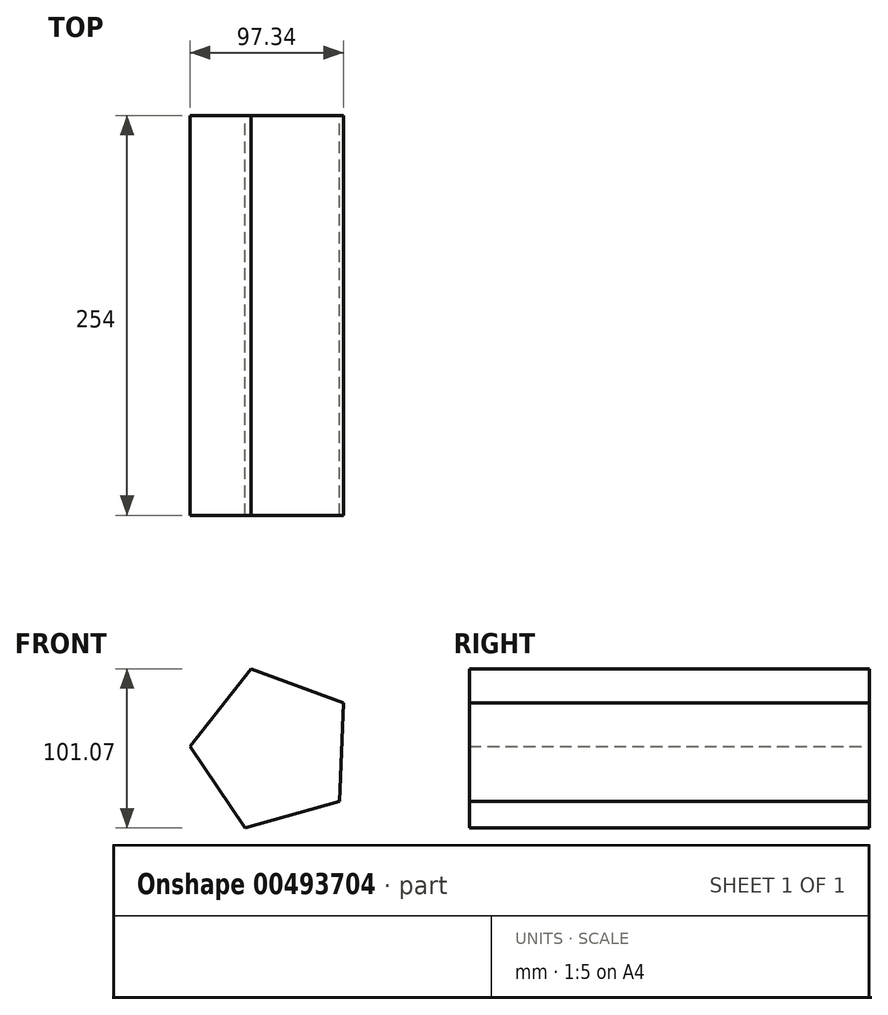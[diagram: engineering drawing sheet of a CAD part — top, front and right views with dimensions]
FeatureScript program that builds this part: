
annotation { "Feature Type Name" : "Feature", "Feature Type Description" : "" }
export const myFeature = defineFeature(function(context is Context, id is Id, definition is map)
    precondition{}
    {
        {
            var Q0;
            Q0=qCreatedBy(makeId("Front.planeOp"),FACE);
            var sketch = newSketch(context, id + "F0", { "sketchPlane" : qUnion([Q0])});
            skCircle(sketch, "E0.cCircle", {"center": v(0, 0) * mm, "radius": 43.02 * mm, "construction": true});
            skLineSegment(sketch, "E0.0", {"start": v(-14.46, 51.17) * mm, "end": v(44.2, 29.57) * mm});
            skLineSegment(sketch, "E0.1", {"start": v(44.2, 29.57) * mm, "end": v(41.78, -32.9) * mm});
            skLineSegment(sketch, "E0.2", {"start": v(41.78, -32.9) * mm, "end": v(-18.37, -49.9) * mm});
            skLineSegment(sketch, "E0.3", {"start": v(-18.37, -49.9) * mm, "end": v(-53.14, 2.06) * mm});
            skLineSegment(sketch, "E0.4", {"start": v(-53.14, 2.06) * mm, "end": v(-14.46, 51.17) * mm});
            skPoint(sketch, "E0.0.midPoint", {"position": v(14.87, 40.37) * mm});
            skSolve(sketch);
        }
        {
            var Q0;
            Q0=makeQuery(id+"F0.imprint","IMPRINT",FACE,{"disambiguationData":[TD([[makeQuery(id+"F0.imprint","IMPRINT",EDGE,{"derivedFrom":sQuery(id+"F0.wireOp",EDGE,"E0.0")}),-1.0]])]});
            extrude(context, id + "F1", {"entities" : qUnion([Q0]), "depth" : 254 * mm});
        }
    });
